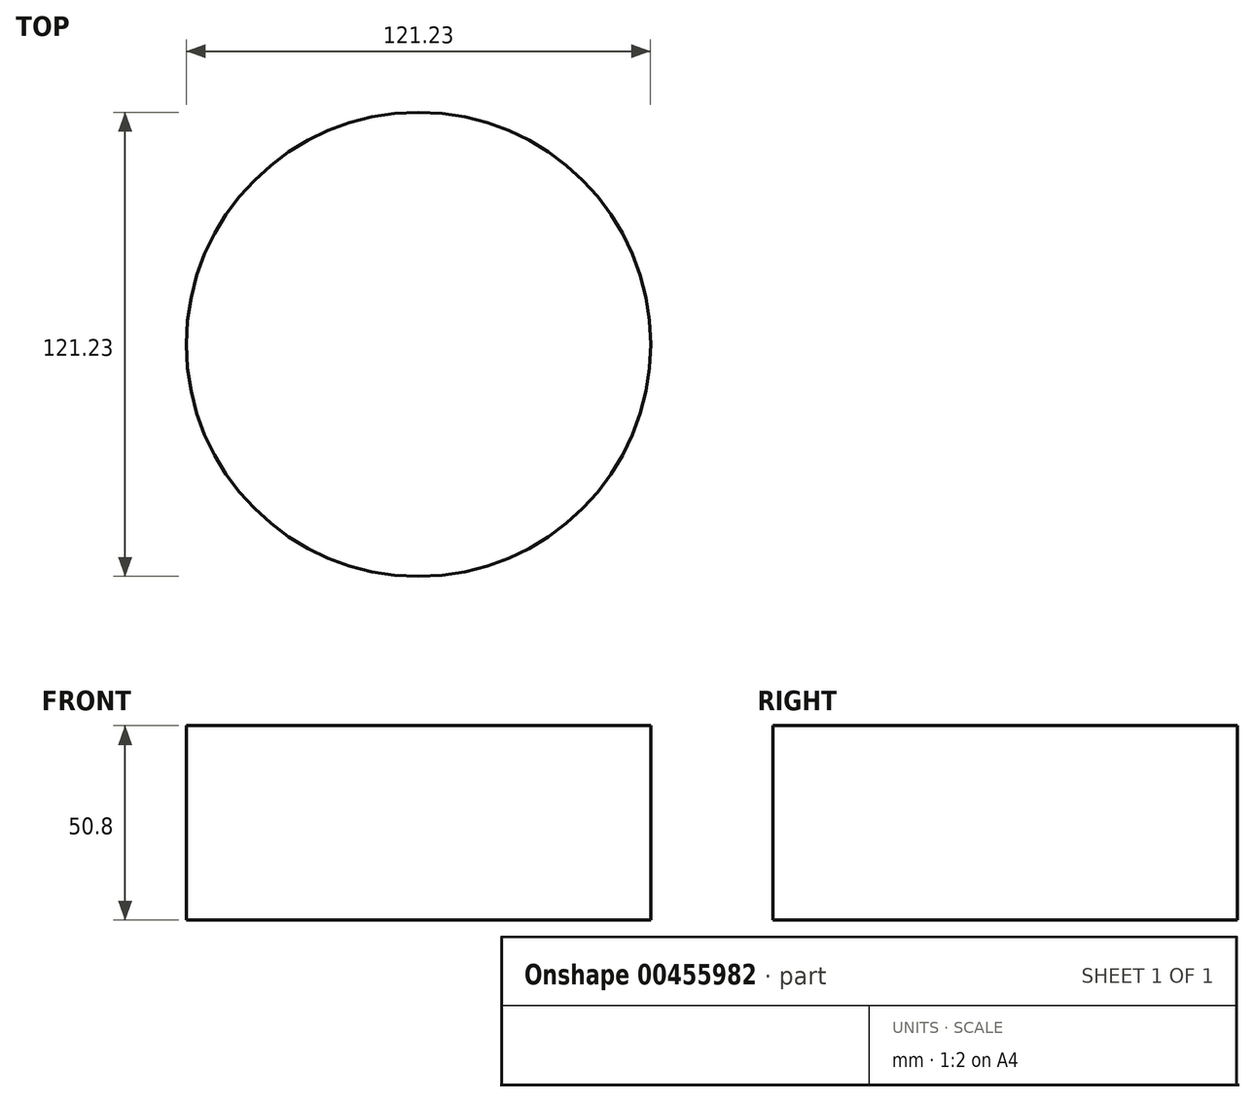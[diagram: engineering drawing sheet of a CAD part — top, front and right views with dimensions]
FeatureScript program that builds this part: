
annotation { "Feature Type Name" : "Feature", "Feature Type Description" : "" }
export const myFeature = defineFeature(function(context is Context, id is Id, definition is map)
    precondition{}
    {
        {
            var Q0;
            Q0=qCreatedBy(makeId("Top.planeOp"),FACE);
            var sketch = newSketch(context, id + "F0", { "sketchPlane" : qUnion([Q0])});
            skCircle(sketch, "E0", {"center": v(-17.46, 27.36) * mm, "radius": 60.61 * mm});
            skSolve(sketch);
        }
        {
            var Q0;
            Q0 = qSketchRegion(id + "F0", true);
            extrude(context, id + "F1", {"entities" : qUnion([Q0]), "depth" : 50.8 * mm});
        }
    });
